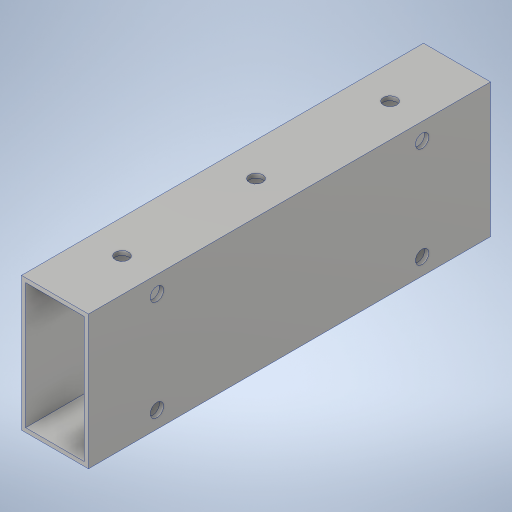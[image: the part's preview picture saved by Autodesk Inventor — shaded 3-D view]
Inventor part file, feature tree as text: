
AUTODESK INVENTOR PART (.ipt)
format: ipt  version: 2023.4 (Build 274418000, 418)  size: 251,904 bytes
history: native  units: in
note: dims shown in document units (in); Inventor stores cm internally (conversion verified against a paired STEP export)
features: hole x3, sketch x3, extrude x1, projected_geometry x1
ambient origin geometry x8: Origin, YZ Plane, XZ Plane, XY Plane, X Axis, Y Axis, Z Axis, Center Point
bodies: Solid1 (feature_tree)
feature tree (8):
  extrude  "Extrusion1"  Depth=4.0in
  hole  "Hole1"  [1 undecoded]
  hole  "Hole3"  [1 undecoded]
  hole  "Hole2"  [1 undecoded]
  sketch  "Sketch2"  dims[d4=0.0in d5=4.0in]
  projected_geometry  "Projected Loop1"
  sketch  "Sketch3"  dims[d6=0.201in d7=0.75in d8=0.385in d9=0.25in d10=0.5635in d11=1.0in d12=0.8108in d14=4.7244in]
  sketch  "Sketch4"  dims[d15=3.7402in d16=4.2323in d17=1.5in d18=0.156in d19=0.38in d20=0.375in d21=0.25in d22=0.5635in d23=1.0in d24=0.8108in d25=4.2323in d28=1.5in d29=0.201in d30=0.38in d31=0.385in d32=0.25in d33=0.5635in d34=1.0in d35=0.8108in]
note: 3 required parameter values undecoded (feature->parameter linkage not recoverable at this tier; creation-order binding heuristic only, values carry confidence <= 0.55)
